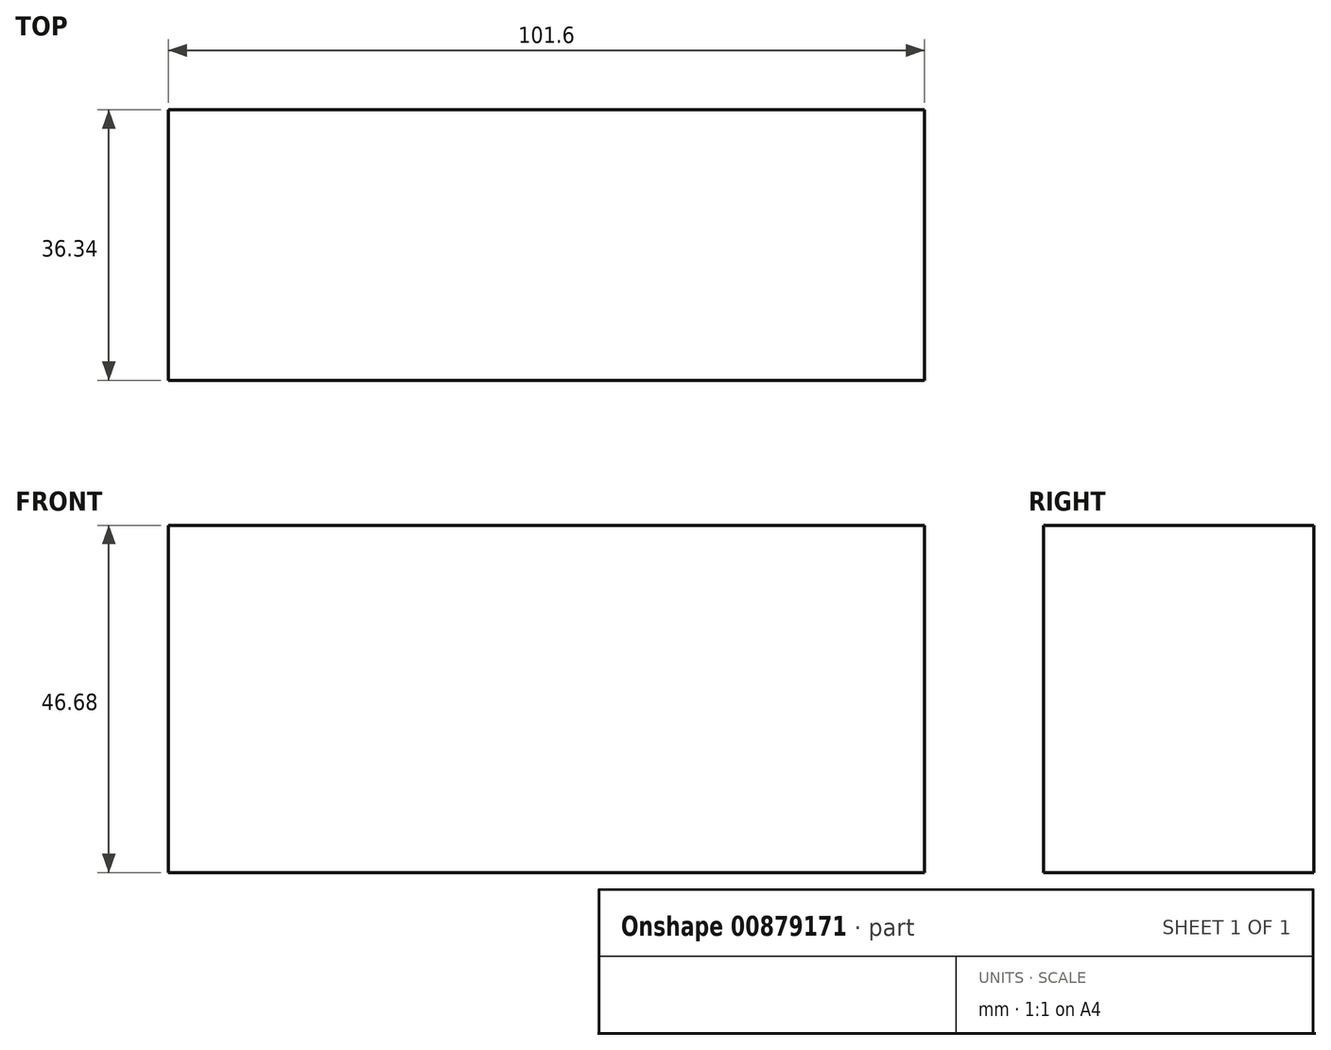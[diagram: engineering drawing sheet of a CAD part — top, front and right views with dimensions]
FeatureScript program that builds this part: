
annotation { "Feature Type Name" : "Feature", "Feature Type Description" : "" }
export const myFeature = defineFeature(function(context is Context, id is Id, definition is map)
    precondition{}
    {
        {
            var Q0;
            Q0=qCreatedBy(makeId("Right.planeOp"),FACE);
            var sketch = newSketch(context, id + "F0", { "sketchPlane" : qUnion([Q0])});
            skLineSegment(sketch, "E0", {"start": v(0, 0) * mm, "end": v(0, -46.68) * mm});
            skLineSegment(sketch, "E1", {"start": v(0, 0) * mm, "end": v(36.34, 0) * mm});
            skLineSegment(sketch, "E2", {"start": v(0, -46.68) * mm, "end": v(36.34, -46.68) * mm});
            skLineSegment(sketch, "E3", {"start": v(36.34, -46.68) * mm, "end": v(36.34, 0) * mm});
            skSolve(sketch);
        }
        {
            var Q0;
            Q0=makeQuery(id+"F0.imprint","IMPRINT",FACE,{"disambiguationData":[TD([[makeQuery(id+"F0.imprint","IMPRINT",EDGE,{"derivedFrom":sQuery(id+"F0.wireOp",EDGE,"E0")}),1.0]])]});
            extrude(context, id + "F1", {"entities" : qUnion([Q0]), "endBound" : BoundingType.SYMMETRIC, "depth" : 101.6 * mm, "offsetDistance" : 25.4 * mm});
        }
    });
